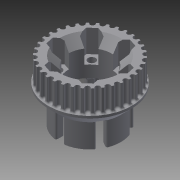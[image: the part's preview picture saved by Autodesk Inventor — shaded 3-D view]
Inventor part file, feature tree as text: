
AUTODESK INVENTOR PART (.ipt)
format: ipt  version: 2014 (Build 180170000, 170)  size: 1,960,448 bytes
history: native  units: in
note: dims shown in document units (in); Inventor stores cm internally (conversion verified against a paired STEP export)
features: extrude x5, other x4, sketch x4, chamfer x2, fillet x2, move_body x1, projected_geometry x1
ambient origin geometry x8: Origin, YZ Plane, XZ Plane, XY Plane, X Axis, Y Axis, Z Axis, Center Point
bodies: Solid1 (feature_tree), Solid2 (feature_tree)
feature tree (19):
  other  "wheelinsertsketch.ipt"
  other  "34t_pulley.ipt"
  extrude  "Extrusion1"  Depth=0.65in TaperAngle=0.0deg
  extrude  "Extrusion2"  Depth=0.3in TaperAngle=0.0deg
  chamfer  "Chamfer1"  Distance=0.24in Angle=45.0deg
  fillet  "Fillet4"  Radius=0.075in
  move_body  "Move Body1"
  sketch  "Sketch2"  dims[d3=2.15in d4=0.3in d5=0.0in d6=0.24in d7=0.125in d8=45.0deg d12=0.075in]
  extrude  "this is hella sketch"  TaperAngle=90.0deg  [1 undecoded]
  extrude  "Extrusion4"  Depth=0.375in TaperAngle=0.0deg
  fillet  "Fillet5"  Radius=0.5906in
  sketch  "Sketch4"  dims[d15=0.0in d16=-2.0in d17=0.0in d18=1.0in d19=0.0in d20=0.5906in d21=0.0in d22=0.05in d23=0.375in d24=0.23in d25=0.125in d26=45.0deg d27=2.3622in d29=360.0deg d31=0.5906in d32=0.0in]
  chamfer  "Chamfer2"  Distance=0.05in
  extrude  "Extrusion5"  Depth=0.375in
  sketch  "Sketch1"  dims[d0=0.3937in d1=0.65in d2=0.0in]
  other  "Solid1::34t_pulley.ipt"
  other  "TaggingFeature1"
  projected_geometry  "Projected Loop1"
  sketch  "Sketch3"  dims[d13=0.3937in d14=90.0deg]
note: 1 required parameter value undecoded (feature->parameter linkage not recoverable at this tier; creation-order binding heuristic only, values carry confidence <= 0.55)
